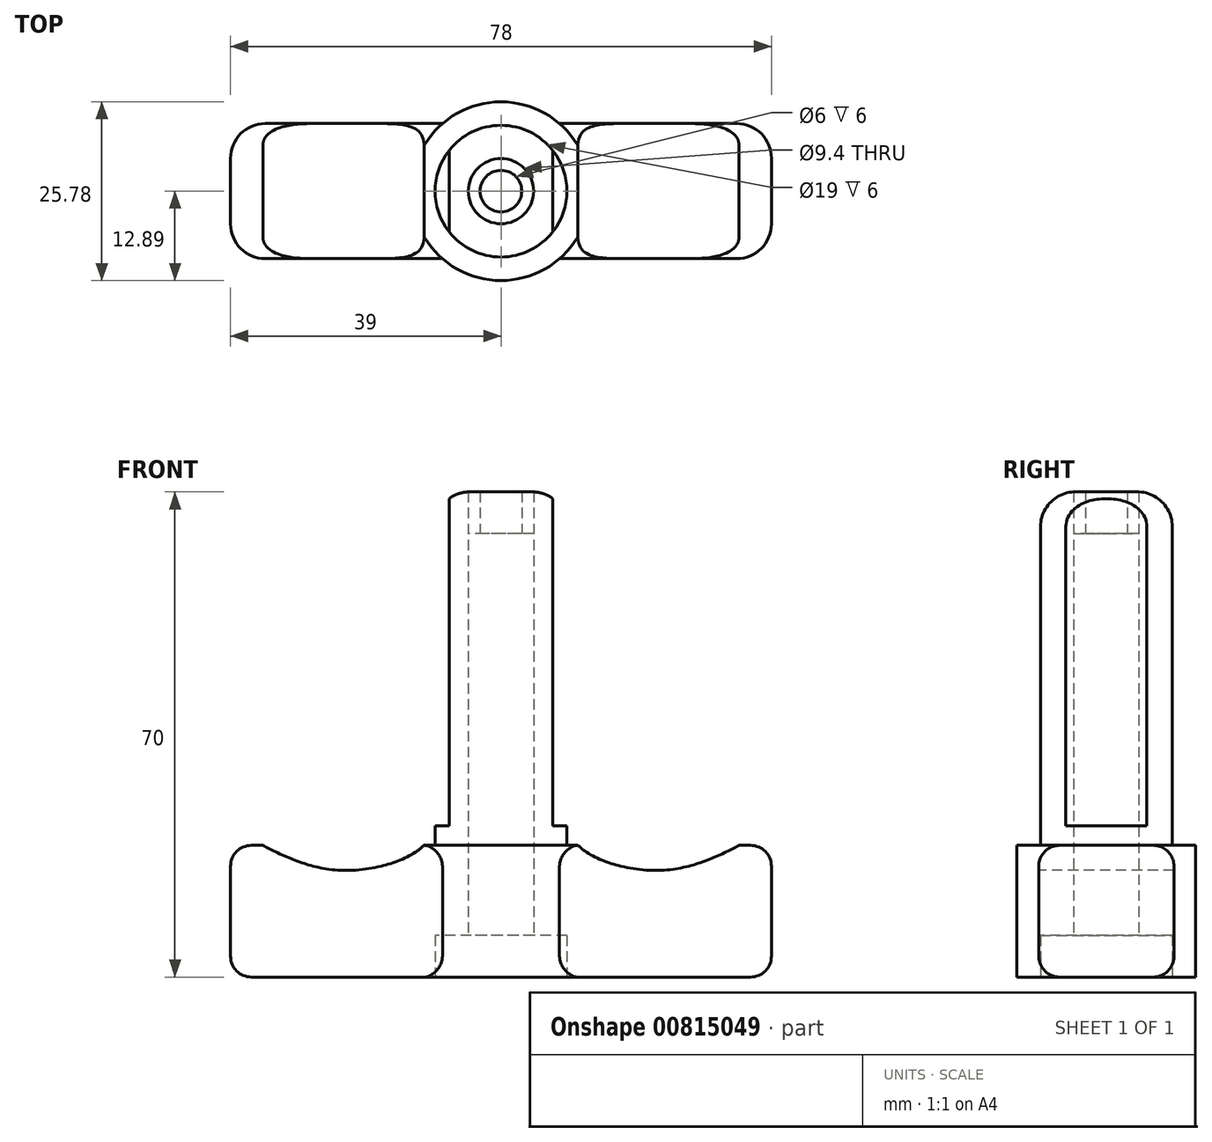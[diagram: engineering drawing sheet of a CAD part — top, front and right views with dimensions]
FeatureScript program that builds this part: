
annotation { "Feature Type Name" : "Feature", "Feature Type Description" : "" }
export const myFeature = defineFeature(function(context is Context, id is Id, definition is map)
    precondition{}
    {
        {
            var Q0;
            Q0=qCreatedBy(makeId("Top.planeOp"),FACE);
            var sketch = newSketch(context, id + "F0", { "sketchPlane" : qUnion([Q0])});
            skCircle(sketch, "E0", {"center": v(0, 0) * mm, "radius": 4.7 * mm});
            skCircle(sketch, "E1", {"center": v(0, 0) * mm, "radius": 3 * mm});
            skLineSegment(sketch, "E2.bottom", {"start": v(-34, 9.75) * mm, "end": v(-8.44, 9.75) * mm});
            skLineSegment(sketch, "E2.top", {"start": v(-34, -9.75) * mm, "end": v(-8.44, -9.75) * mm});
            skLineSegment(sketch, "E2.left", {"start": v(-39, 4.75) * mm, "end": v(-39, -4.75) * mm});
            skLineSegment(sketch, "E2.right", {"start": v(39, 4.75) * mm, "end": v(39, -4.75) * mm});
            skPoint(sketch, "E3.visualSharp", {"position": v(-39, 9.75) * mm});
            skArc(sketch, "E3.filletArc", {"start": v(-34, 9.75) * mm, "mid": v(-37.54, 8.29) * mm, "end": v(-39, 4.75) * mm});
            skPoint(sketch, "E4.visualSharp", {"position": v(-39, -9.75) * mm});
            skArc(sketch, "E4.filletArc", {"start": v(-39, -4.75) * mm, "mid": v(-37.54, -8.29) * mm, "end": v(-34, -9.75) * mm});
            skPoint(sketch, "E5.visualSharp", {"position": v(39, 9.75) * mm});
            skArc(sketch, "E5.filletArc", {"start": v(39, 4.75) * mm, "mid": v(37.54, 8.29) * mm, "end": v(34, 9.75) * mm});
            skPoint(sketch, "E6.visualSharp", {"position": v(39, -9.75) * mm});
            skArc(sketch, "E6.filletArc", {"start": v(34, -9.75) * mm, "mid": v(37.54, -8.29) * mm, "end": v(39, -4.75) * mm});
            skCircle(sketch, "E7", {"center": v(0, 0) * mm, "radius": 9.5 * mm});
            skArc(sketch, "E8", {"start": v(-8.44, -9.75) * mm, "mid": v(0, -12.9) * mm, "end": v(8.44, -9.75) * mm});
            skArc(sketch, "E9.trimOffspring", {"start": v(8.44, 9.75) * mm, "mid": v(0, 12.9) * mm, "end": v(-8.44, 9.75) * mm});
            skLineSegment(sketch, "E10.trimOffspring", {"start": v(8.44, 9.75) * mm, "end": v(34, 9.75) * mm});
            skLineSegment(sketch, "E11.trimOffspring", {"start": v(8.44, -9.75) * mm, "end": v(34, -9.75) * mm});
            skSolve(sketch);
        }
        {
            var Q0;
            Q0=makeQuery(id+"F0.imprint","IMPRINT",FACE,{"disambiguationData":[TD([[makeQuery(id+"F0.imprint","IMPRINT",EDGE,{"derivedFrom":sQuery(id+"F0.wireOp",EDGE,"E0")}),-1.0]])]});
            extrude(context, id + "F1", {"entities" : qUnion([Q0]), "depth" : 64 * mm, "offsetDistance" : 25 * mm});
        }
        {
            var Q0;
            Q0=makeQuery(id+"F0.imprint","IMPRINT",FACE,{"disambiguationData":[TD([[makeQuery(id+"F0.imprint","IMPRINT",EDGE,{"derivedFrom":sQuery(id+"F0.wireOp",EDGE,"E2.bottom")}),-1.0]])]});
            extrude(context, id + "F2", {"entities" : qUnion([Q0]), "operationType" : NewBodyOperationType.ADD, "depth" : 13 * mm, "offsetDistance" : 25 * mm, "hasSecondDirection" : true, "secondDirectionOppositeDirection" : true, "secondDirectionDepth" : 6 * mm});
        }
        {
            var Q0;
            Q0=makeQuery(id+"F0.imprint","IMPRINT",FACE,{"disambiguationData":[TD([[makeQuery(id+"F0.imprint","IMPRINT",EDGE,{"derivedFrom":sQuery(id+"F0.wireOp",EDGE,"E0")}),1.0]])]});
            extrude(context, id + "F3", {"entities" : qUnion([Q0]), "depth" : 6 * mm, "offsetDistance" : 25 * mm});
        }
        {
            var Q0;
            Q0=makeQuery(id+"F3.opExtrude","SWEPT_BODY",BODY,{"disambiguationData":[OSD([sQuery(id+"F0.wireOp",EDGE,"E0"),sQuery(id+"F0.wireOp",EDGE,"E1")])]});
            transform(context, id + "F4", {"entities" : qUnion([Q0]), "transformType" : TransformType.TRANSLATION_3D, "dx" : 0 * mm, "dy" : 0 * mm, "dz" : 58 * mm, "makeCopy" : false});
        }
        {
            var Q0;
            Q0=makeQuery(id+"F2.opExtrude","CAP_EDGE",EDGE,{"disambiguationData":[OSD([sQuery(id+"F0.wireOp",EDGE,"E7")])],"isStart":false});
            var Q1;
            Q1=makeQuery(id+"F2.opExtrude","CAP_EDGE",EDGE,{"disambiguationData":[OSD([sQuery(id+"F0.wireOp",EDGE,"E2.bottom")])],"isStart":false});
            var Q2;
            Q2=makeQuery(id+"F2.opExtrude","CAP_EDGE",EDGE,{"disambiguationData":[OSD([sQuery(id+"F0.wireOp",EDGE,"E5.filletArc")])],"isStart":false});
            var Q3;
            Q3=makeQuery(id+"F2.opExtrude","CAP_EDGE",EDGE,{"disambiguationData":[OSD([sQuery(id+"F0.wireOp",EDGE,"E2.right")])],"isStart":false});
            var Q4;
            Q4=makeQuery(id+"F2.opExtrude","CAP_EDGE",EDGE,{"disambiguationData":[OSD([sQuery(id+"F0.wireOp",EDGE,"E6.filletArc")])],"isStart":false});
            var Q5;
            Q5=makeQuery(id+"F2.opExtrude","CAP_EDGE",EDGE,{"disambiguationData":[OSD([sQuery(id+"F0.wireOp",EDGE,"E2.top")])],"isStart":false});
            var Q6;
            Q6=makeQuery(id+"F2.opExtrude","CAP_EDGE",EDGE,{"disambiguationData":[OSD([sQuery(id+"F0.wireOp",EDGE,"E4.filletArc")])],"isStart":false});
            var Q7;
            Q7=makeQuery(id+"F2.opExtrude","CAP_EDGE",EDGE,{"disambiguationData":[OSD([sQuery(id+"F0.wireOp",EDGE,"E2.left")])],"isStart":false});
            var Q8;
            Q8=makeQuery(id+"F2.opExtrude","CAP_EDGE",EDGE,{"disambiguationData":[OSD([sQuery(id+"F0.wireOp",EDGE,"E3.filletArc")])],"isStart":false});
            var Q9;
            Q9=makeQuery(id+"F2.opExtrude","CAP_EDGE",EDGE,{"disambiguationData":[OSD([sQuery(id+"F0.wireOp",EDGE,"E2.bottom")])],"isStart":true});
            var Q10;
            Q10=makeQuery(id+"F2.opExtrude","CAP_EDGE",EDGE,{"disambiguationData":[OSD([sQuery(id+"F0.wireOp",EDGE,"E3.filletArc")])],"isStart":true});
            var Q11;
            Q11=makeQuery(id+"F2.opExtrude","CAP_EDGE",EDGE,{"disambiguationData":[OSD([sQuery(id+"F0.wireOp",EDGE,"E10.trimOffspring")])],"isStart":true});
            fillet(context, id + "F5", {"entities" : qUnion([Q0, Q1, Q2, Q3, Q4, Q5, Q6, Q7, Q8, Q9, Q10, Q11]), "radius" : 3 * mm, "tangentPropagation" : true, "allowEdgeOverflow" : false});
        }
        {
            var Q0;
            Q0=makeQuery(id+"F1.opExtrude","CAP_EDGE",EDGE,{"disambiguationData":[OSD([sQuery(id+"F0.wireOp",EDGE,"E7")])],"isStart":false});
            fillet(context, id + "F6", {"entities" : qUnion([Q0]), "radius" : 5 * mm, "tangentPropagation" : true, "allowEdgeOverflow" : false});
        }
        {
            var Q0;
            Q0=qCreatedBy(makeId("Front.planeOp"),FACE);
            var sketch = newSketch(context, id + "F7", { "sketchPlane" : qUnion([Q0])});
            skFitSpline(sketch, "E12", {"points": [v(-36.4, 15.15) * mm, v(-35.35, 13.61) * mm, v(-31.56, 11.63) * mm, v(-23.13, 9.4) * mm, v(-11.68, 12.5) * mm, v(-10.93, 15.84) * mm, v(-36.4, 15.15) * mm]});
            skLineSegment(sketch, "E13", {"start": v(0, -30.8) * mm, "end": v(0, 50.62) * mm, "construction": true});
            skFitSpline(sketch, "E14.MirrorC", {"points": [v(36.4, 15.15) * mm, v(35.35, 13.61) * mm, v(31.56, 11.63) * mm, v(23.13, 9.4) * mm, v(11.68, 12.5) * mm, v(10.93, 15.84) * mm, v(36.4, 15.15) * mm]});
            skLineSegment(sketch, "E15.bottom", {"start": v(-27.97, 65.24) * mm, "end": v(-7.49, 65.24) * mm});
            skLineSegment(sketch, "E15.top", {"start": v(-27.97, 15.84) * mm, "end": v(-7.49, 15.84) * mm});
            skLineSegment(sketch, "E15.left", {"start": v(-27.97, 65.24) * mm, "end": v(-27.97, 15.84) * mm});
            skLineSegment(sketch, "E15.right", {"start": v(-7.49, 65.24) * mm, "end": v(-7.49, 15.84) * mm});
            skLineSegment(sketch, "E16.MirrorCS", {"start": v(27.97, 65.24) * mm, "end": v(27.97, 15.84) * mm});
            skLineSegment(sketch, "E17.MirrorCS", {"start": v(27.97, 65.24) * mm, "end": v(7.49, 65.24) * mm});
            skLineSegment(sketch, "E18.MirrorCS", {"start": v(7.49, 65.24) * mm, "end": v(7.49, 15.84) * mm});
            skLineSegment(sketch, "E19.MirrorCS", {"start": v(27.97, 15.84) * mm, "end": v(7.49, 15.84) * mm});
            skSolve(sketch);
        }
        {
            var Q0;
            Q0=makeQuery(id+"F7.imprint","IMPRINT",FACE,{"disambiguationData":[TD([[makeQuery(id+"F7.imprint","IMPRINT",EDGE,{"derivedFrom":sQuery(id+"F7.wireOp",EDGE,"E12")}),1.0]])]});
            var Q1;
            Q1=makeQuery(id+"F7.imprint","IMPRINT",FACE,{"disambiguationData":[TD([[makeQuery(id+"F7.imprint","IMPRINT",EDGE,{"derivedFrom":sQuery(id+"F7.wireOp",EDGE,"E14.MirrorC")}),-1.0]])]});
            var Q2;
            {var subQ1=sQuery(id+"F7.wireOp",EDGE,"E15.bottom");Q2=makeQuery(id+"F7.imprint","IMPRINT",FACE,{"disambiguationData":[TD([[makeQuery(id+"F7.imprint","IMPRINT",EDGE,{"derivedFrom":subQ1}),-1.0]])]});}
            var Q3;
            {var subQ6=sQuery(id+"F7.wireOp",EDGE,"E17.MirrorCS");Q3=makeQuery(id+"F7.imprint","IMPRINT",FACE,{"disambiguationData":[TD([[makeQuery(id+"F7.imprint","IMPRINT",EDGE,{"derivedFrom":subQ6}),1.0]])]});}
            extrude(context, id + "F8", {"entities" : qUnion([Q0, Q1, Q2, Q3]), "operationType" : NewBodyOperationType.REMOVE, "endBound" : BoundingType.SYMMETRIC, "oppositeDirection" : true, "depth" : 25 * mm, "offsetDistance" : 25 * mm});
        }
    });
